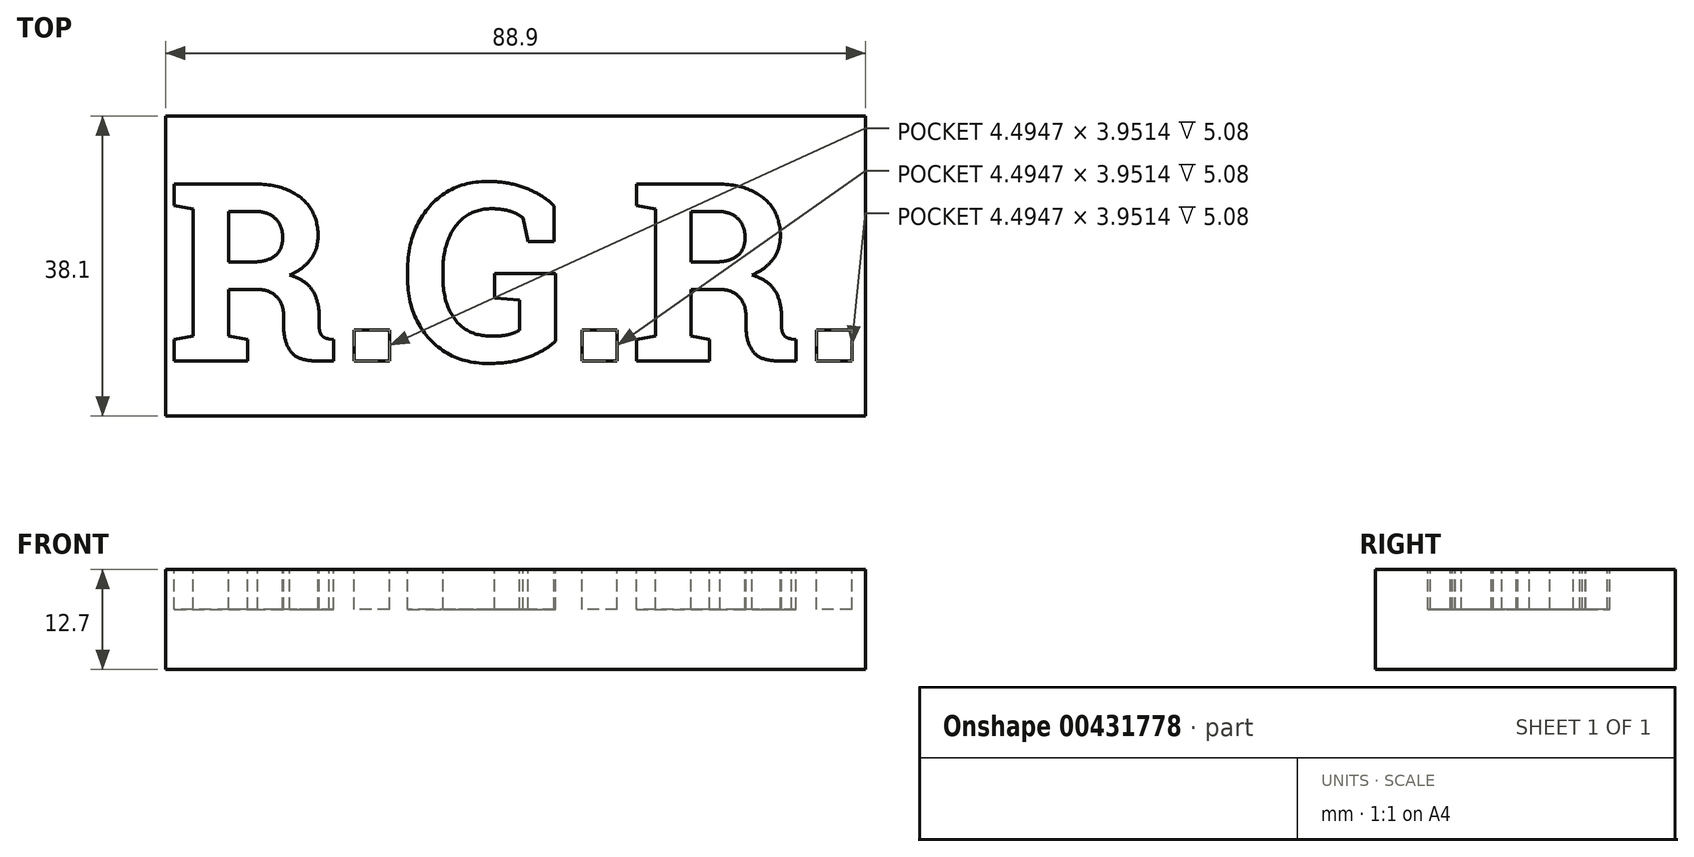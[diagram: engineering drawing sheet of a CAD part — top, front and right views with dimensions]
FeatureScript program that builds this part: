
annotation { "Feature Type Name" : "Feature", "Feature Type Description" : "" }
export const myFeature = defineFeature(function(context is Context, id is Id, definition is map)
    precondition{}
    {
        {
            var Q0;
            Q0=qCreatedBy(makeId("Top.planeOp"),FACE);
            var sketch = newSketch(context, id + "F0", { "sketchPlane" : qUnion([Q0])});
            skLineSegment(sketch, "E0.bottom", {"start": v(-44.23, 22.09) * mm, "end": v(44.67, 22.09) * mm});
            skLineSegment(sketch, "E0.top", {"start": v(-44.23, -16.01) * mm, "end": v(44.67, -16.01) * mm});
            skLineSegment(sketch, "E0.left", {"start": v(-44.23, 22.09) * mm, "end": v(-44.23, -16.01) * mm});
            skLineSegment(sketch, "E0.right", {"start": v(44.67, 22.09) * mm, "end": v(44.67, -16.01) * mm});
            skSolve(sketch);
        }
        {
            var Q0;
            Q0 = qSketchRegion(id + "F0", true);
            extrude(context, id + "F1", {"entities" : qUnion([Q0]), "depth" : 12.7 * mm});
        }
        {
            var Q0;
            Q0=makeQuery(id+"F1.opExtrude","CAP_FACE",FACE,{"disambiguationData":[OSD([sQuery(id+"F0.wireOp",EDGE,"E0.bottom"),sQuery(id+"F0.wireOp",EDGE,"E0.top"),sQuery(id+"F0.wireOp",EDGE,"E0.left"),sQuery(id+"F0.wireOp",EDGE,"E0.right")])],"isStart":false});
            var sketch = newSketch(context, id + "F2", { "sketchPlane" : qUnion([Q0])});
            skText(sketch, "E1", { "text": "R.G.R.", "fontName": "RobotoSlab-Bold.ttf"});
            const initialGuessF2  = {"E1": [-0.04402, -0.00901, 1, 0, 0.02276]};
            skSetInitialGuess(sketch, initialGuessF2);
            skSolve(sketch);
        }
        {
            var Q0;
            Q0 = qSketchRegion(id + "F2", true);
            extrude(context, id + "F3", {"entities" : qUnion([Q0]), "operationType" : NewBodyOperationType.REMOVE, "oppositeDirection" : true, "depth" : 5.08 * mm});
        }
    });
